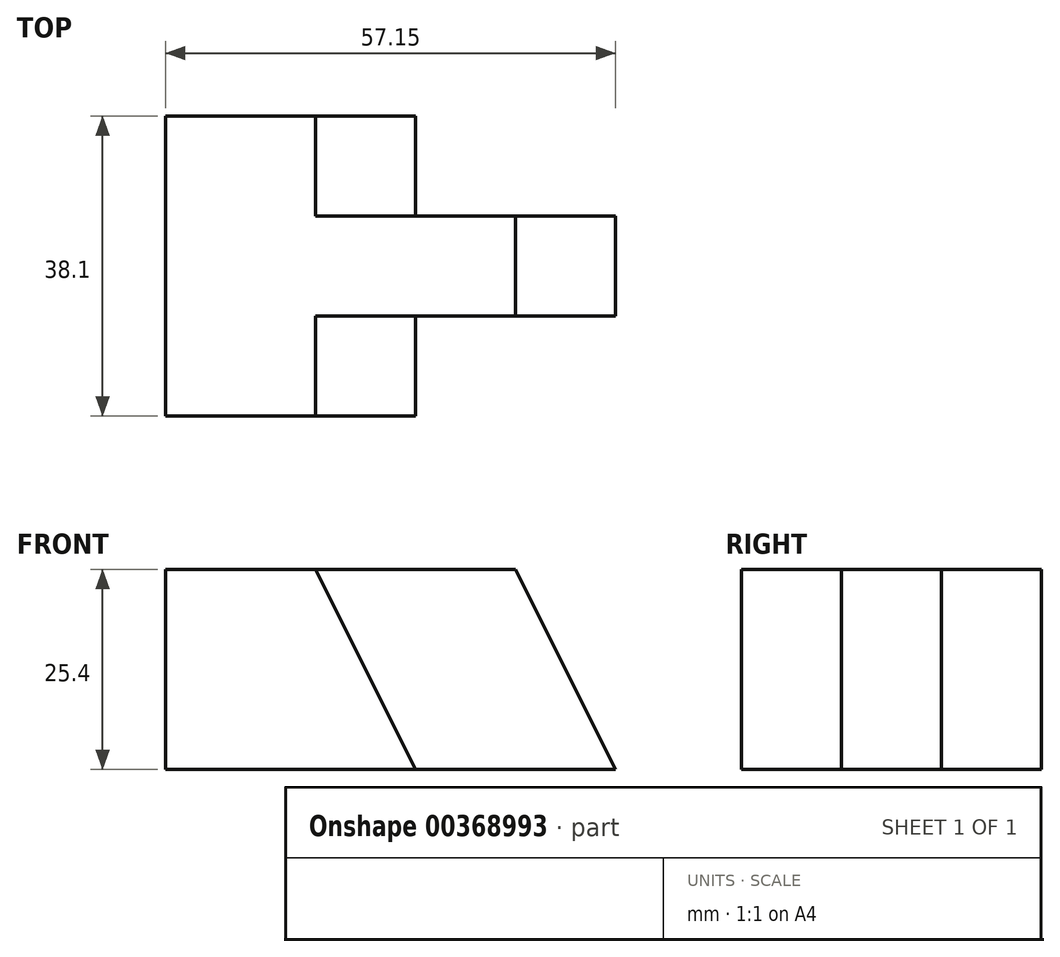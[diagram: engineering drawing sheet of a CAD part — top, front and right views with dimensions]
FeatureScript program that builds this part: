
annotation { "Feature Type Name" : "Feature", "Feature Type Description" : "" }
export const myFeature = defineFeature(function(context is Context, id is Id, definition is map)
    precondition{}
    {
        {
            var Q0;
            Q0=qCreatedBy(makeId("Front.planeOp"),FACE);
            var sketch = newSketch(context, id + "F0", { "sketchPlane" : qUnion([Q0])});
            skLineSegment(sketch, "E0", {"start": v(0, 0) * mm, "end": v(57.15, 0) * mm});
            skLineSegment(sketch, "E1", {"start": v(57.15, 0) * mm, "end": v(57.15, 25.4) * mm});
            skLineSegment(sketch, "E2", {"start": v(57.15, 25.4) * mm, "end": v(0, 25.4) * mm});
            skLineSegment(sketch, "E3", {"start": v(0, 25.4) * mm, "end": v(0, 0) * mm});
            skSolve(sketch);
        }
        {
            var Q0;
            Q0 = qSketchRegion(id + "F0", true);
            extrude(context, id + "F1", {"entities" : qUnion([Q0]), "depth" : 38.1 * mm});
        }
        {
            var Q0;
            Q0=makeQuery(id+"F1.opExtrude","CAP_FACE",FACE,{"disambiguationData":[OSD([sQuery(id+"F0.wireOp",EDGE,"E0"),sQuery(id+"F0.wireOp",EDGE,"E1"),sQuery(id+"F0.wireOp",EDGE,"E2"),sQuery(id+"F0.wireOp",EDGE,"E3")])],"isStart":false});
            var sketch = newSketch(context, id + "F2", { "sketchPlane" : qUnion([Q0])});
            skLineSegment(sketch, "E4", {"start": v(44.45, 25.4) * mm, "end": v(57.15, 0) * mm});
            skLineSegment(sketch, "E5", {"start": v(57.15, 0) * mm, "end": v(57.15, 25.4) * mm});
            skLineSegment(sketch, "E6", {"start": v(57.15, 25.4) * mm, "end": v(44.45, 25.4) * mm});
            skSolve(sketch);
        }
        {
            var Q0;
            Q0=makeQuery(id+"F2.imprint","IMPRINT",FACE,{"disambiguationData":[TD([[makeQuery(id+"F2.imprint","IMPRINT",EDGE,{"derivedFrom":sQuery(id+"F2.wireOp",EDGE,"E4")}),1.0]])]});
            extrude(context, id + "F3", {"entities" : qUnion([Q0]), "operationType" : NewBodyOperationType.REMOVE, "oppositeDirection" : true, "depth" : 38.1 * mm});
        }
        {
            var Q0;
            Q0=makeQuery(id+"F1.opExtrude","CAP_FACE",FACE,{"disambiguationData":[OSD([sQuery(id+"F0.wireOp",EDGE,"E0"),sQuery(id+"F0.wireOp",EDGE,"E1"),sQuery(id+"F0.wireOp",EDGE,"E2"),sQuery(id+"F0.wireOp",EDGE,"E3")])],"isStart":false});
            var sketch = newSketch(context, id + "F4", { "sketchPlane" : qUnion([Q0])});
            skLineSegment(sketch, "E7", {"start": v(44.45, 25.4) * mm, "end": v(19.05, 25.4) * mm});
            skLineSegment(sketch, "E8", {"start": v(19.05, 25.4) * mm, "end": v(31.75, 0) * mm});
            skLineSegment(sketch, "E9", {"start": v(31.75, 0) * mm, "end": v(57.15, 0) * mm});
            skLineSegment(sketch, "E10", {"start": v(57.15, 0) * mm, "end": v(44.45, 25.4) * mm});
            skSolve(sketch);
        }
        {
            var Q0;
            Q0=makeQuery(id+"F4.imprint","IMPRINT",FACE,{"disambiguationData":[TD([[makeQuery(id+"F4.imprint","IMPRINT",EDGE,{"derivedFrom":sQuery(id+"F4.wireOp",EDGE,"E7")}),1.0]])]});
            extrude(context, id + "F5", {"entities" : qUnion([Q0]), "operationType" : NewBodyOperationType.REMOVE, "oppositeDirection" : true, "depth" : 12.7 * mm});
        }
        {
            var Q0;
            Q0=makeQuery(id+"F1.opExtrude","CAP_FACE",FACE,{"disambiguationData":[OSD([sQuery(id+"F0.wireOp",EDGE,"E0"),sQuery(id+"F0.wireOp",EDGE,"E1"),sQuery(id+"F0.wireOp",EDGE,"E2"),sQuery(id+"F0.wireOp",EDGE,"E3")])],"isStart":true});
            var sketch = newSketch(context, id + "F6", { "sketchPlane" : qUnion([Q0])});
            skLineSegment(sketch, "E11", {"start": v(-19.05, 25.4) * mm, "end": v(-31.75, 0) * mm});
            skLineSegment(sketch, "E12", {"start": v(-31.75, 0) * mm, "end": v(-57.15, 0) * mm});
            skLineSegment(sketch, "E13", {"start": v(-57.15, 0) * mm, "end": v(-44.45, 25.4) * mm});
            skLineSegment(sketch, "E14", {"start": v(-44.45, 25.4) * mm, "end": v(-19.05, 25.4) * mm});
            skSolve(sketch);
        }
        {
            var Q0;
            Q0=makeQuery(id+"F6.imprint","IMPRINT",FACE,{"disambiguationData":[TD([[makeQuery(id+"F6.imprint","IMPRINT",EDGE,{"derivedFrom":sQuery(id+"F6.wireOp",EDGE,"E11")}),-1.0]])]});
            extrude(context, id + "F7", {"entities" : qUnion([Q0]), "operationType" : NewBodyOperationType.REMOVE, "oppositeDirection" : true, "depth" : 12.7 * mm});
        }
    });
